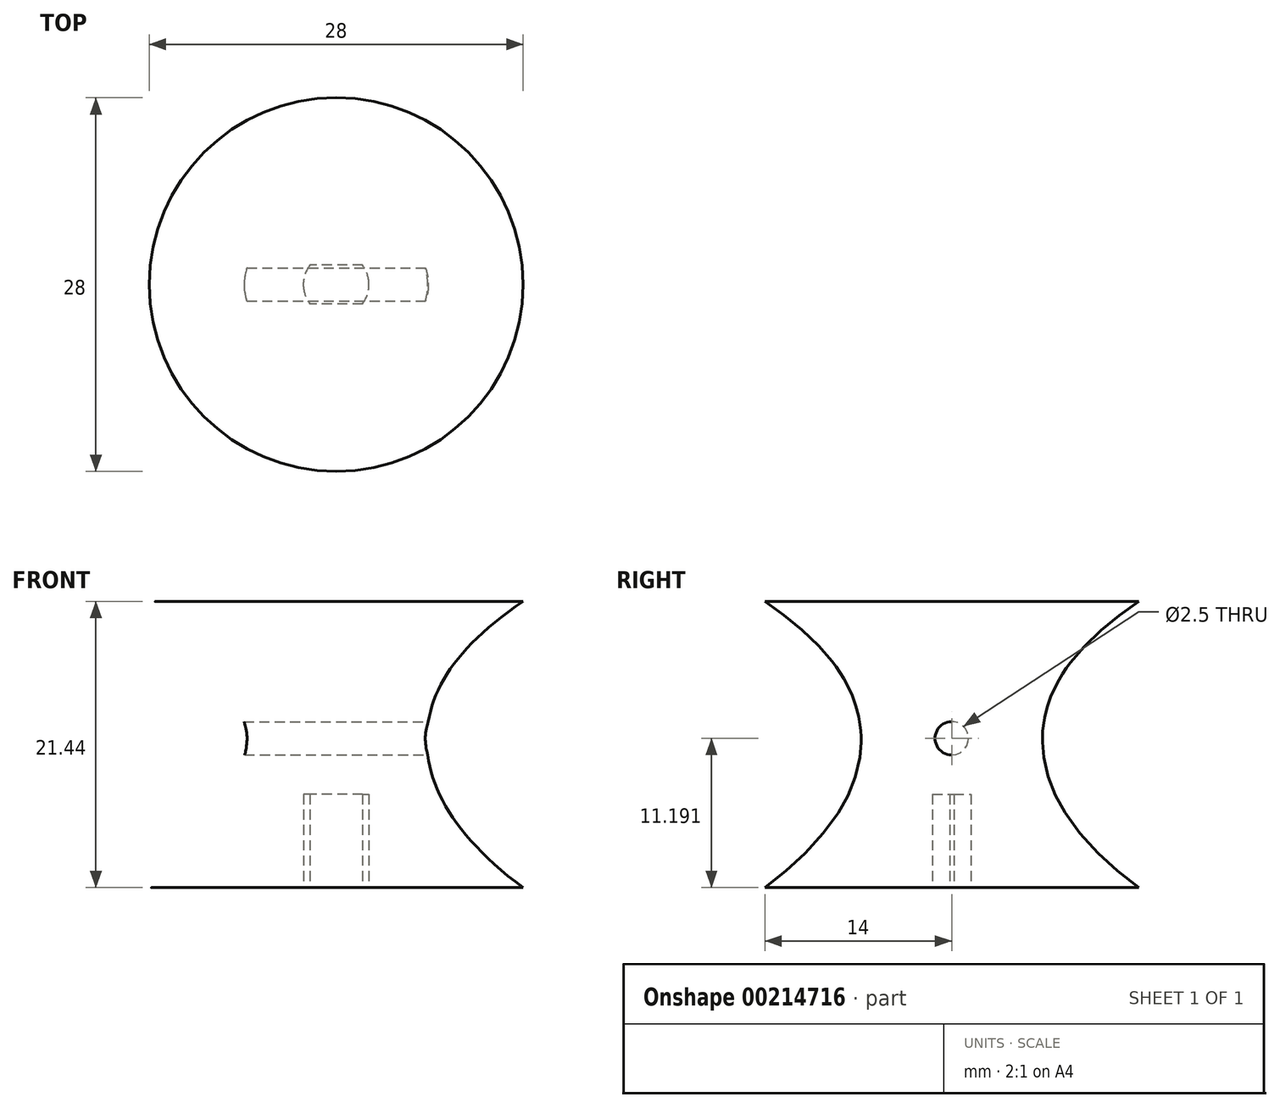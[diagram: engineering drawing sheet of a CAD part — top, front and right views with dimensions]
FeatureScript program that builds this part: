
annotation { "Feature Type Name" : "Feature", "Feature Type Description" : "" }
export const myFeature = defineFeature(function(context is Context, id is Id, definition is map)
    precondition{}
    {
        {
            var Q0;
            Q0=qCreatedBy(makeId("Top.planeOp"),FACE);
            var sketch = newSketch(context, id + "F0", { "sketchPlane" : qUnion([Q0])});
            skCircle(sketch, "E0", {"center": v(0, 0) * mm, "radius": 2.46 * mm});
            skLineSegment(sketch, "E1.bottom", {"start": v(2.45, -1.45) * mm, "end": v(-2.45, -1.45) * mm});
            skLineSegment(sketch, "E1.top", {"start": v(2.45, 1.45) * mm, "end": v(-2.45, 1.45) * mm});
            skLineSegment(sketch, "E1.left", {"start": v(2.45, -1.45) * mm, "end": v(2.45, 1.45) * mm});
            skLineSegment(sketch, "E1.right", {"start": v(-2.45, -1.45) * mm, "end": v(-2.45, 1.45) * mm});
            skSolve(sketch);
        }
        {
            var Q0;
            {var subQ1=sQuery(id+"F0.wireOp",EDGE,"E0");var subQ8=sQuery(id+"F0.wireOp",EDGE,"E1.top");var subQ11=makeQuery(id+"F0.imprint","INTERSECT",VERTEX,{"disambiguationData":[OD(0.0)],"derivedFrom":[subQ1,subQ8]});Q0=makeQuery(id+"F0.imprint","IMPRINT",FACE,{"disambiguationData":[TD([[makeQuery(id+"F0.imprint","IMPRINT",EDGE,{"disambiguationData":[TD([[subQ11,1.0]])],"derivedFrom":subQ1}),1.0]])]});}
            extrude(context, id + "F1", {"entities" : qUnion([Q0]), "depth" : 7 * mm});
        }
        {
            var Q0;
            Q0=qCreatedBy(makeId("Front.planeOp"),FACE);
            var sketch = newSketch(context, id + "F2", { "sketchPlane" : qUnion([Q0])});
            skLineSegment(sketch, "E2", {"start": v(0, 0) * mm, "end": v(-14, 0) * mm});
            skFitSpline(sketch, "E3", {"points": [v(-14, 0) * mm, v(-6.8, 11.2) * mm, v(-14, 21.44) * mm], "startDerivative": vector(30.3, 22.65) * mm, "endDerivative": vector(-30.63, 20.61) * mm});
            skLineSegment(sketch, "E4", {"start": v(-14, 21.44) * mm, "end": v(0, 21.44) * mm});
            skLineSegment(sketch, "E5", {"start": v(0, 21.44) * mm, "end": v(0, 0) * mm});
            skSolve(sketch);
        }
        {
            var Q0;
            Q0 = qSketchRegion(id + "F2", true);
            var Q1;
            Q1=sQuery(id+"F2.wireOp",EDGE,"E5");
            revolve(context, id + "F3", {"entities" : qUnion([Q0]), "axis" : qUnion([Q1]), "revolveType" : RevolveType.FULL});
        }
        {
            var Q0;
            Q0=makeQuery(id+"F1.opExtrude","SWEPT_BODY",BODY,{"disambiguationData":[OSD([sQuery(id+"F0.wireOp",EDGE,"E0"),sQuery(id+"F0.wireOp",EDGE,"E1.bottom"),sQuery(id+"F0.wireOp",EDGE,"E1.top"),sQuery(id+"F0.wireOp",EDGE,"E1.left"),sQuery(id+"F0.wireOp",EDGE,"E1.right")])]});
            var Q1;
            Q1=makeQuery(id+"F3.opRevolve","SWEPT_BODY",BODY,{"disambiguationData":[OSD([sQuery(id+"F2.wireOp",EDGE,"E2"),sQuery(id+"F2.wireOp",EDGE,"E3"),sQuery(id+"F2.wireOp",EDGE,"E4"),sQuery(id+"F2.wireOp",EDGE,"E5")])]});
            booleanBodies(context, id + "F4", {"operationType" : BooleanOperationType.SUBTRACTION, "tools" : qUnion([Q0]), "targets" : qUnion([Q1])});
        }
        {
            var Q0;
            Q0=qCreatedBy(makeId("Right.planeOp"),FACE);
            var sketch = newSketch(context, id + "F5", { "sketchPlane" : qUnion([Q0])});
            skCircle(sketch, "E6", {"center": v(0, 11.2) * mm, "radius": 1.25 * mm});
            skSolve(sketch);
        }
        {
            var Q0;
            Q0 = qSketchRegion(id + "F5", true);
            extrude(context, id + "F6", {"entities" : qUnion([Q0]), "operationType" : NewBodyOperationType.REMOVE, "oppositeDirection" : true, "depth" : 12.7 * mm});
        }
        {
            var Q0;
            Q0=makeQuery(id+"F5.imprint","IMPRINT",FACE,{"disambiguationData":[TD([[makeQuery(id+"F5.imprint","IMPRINT",EDGE,{"derivedFrom":sQuery(id+"F5.wireOp",EDGE,"E6")}),1.0]])]});
            var Q1;
            Q1=sQuery(id+"F5.wireOp",EDGE,"E6");
            extrude(context, id + "F7", {"entities" : qUnion([Q0]), "operationType" : NewBodyOperationType.REMOVE, "surfaceEntities" : qUnion([Q1]), "depth" : 12.7 * mm});
        }
    });
